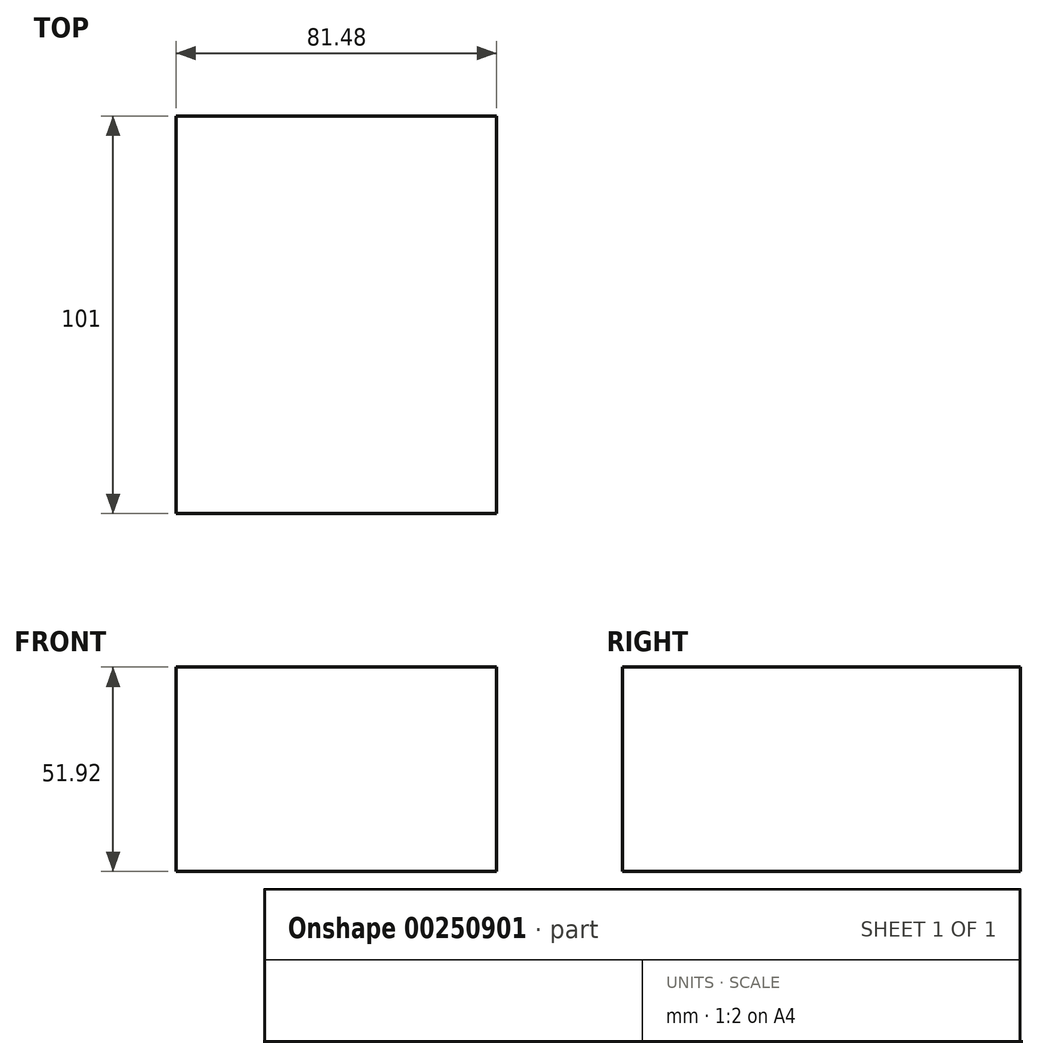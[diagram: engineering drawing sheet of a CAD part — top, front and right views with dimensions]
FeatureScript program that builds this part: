
annotation { "Feature Type Name" : "Feature", "Feature Type Description" : "" }
export const myFeature = defineFeature(function(context is Context, id is Id, definition is map)
    precondition{}
    {
        {
            var Q0;
            Q0=qCreatedBy(makeId("Front.planeOp"),FACE);
            var sketch = newSketch(context, id + "F0", { "sketchPlane" : qUnion([Q0])});
            skLineSegment(sketch, "E0.bottom", {"start": v(40.74, -25.96) * mm, "end": v(-40.74, -25.96) * mm});
            skLineSegment(sketch, "E0.top", {"start": v(40.74, 25.96) * mm, "end": v(-40.74, 25.96) * mm});
            skLineSegment(sketch, "E0.left", {"start": v(40.74, -25.96) * mm, "end": v(40.74, 25.96) * mm});
            skLineSegment(sketch, "E0.right", {"start": v(-40.74, -25.96) * mm, "end": v(-40.74, 25.96) * mm});
            skPoint(sketch, "E0.middle", {"position": v(0, 0) * mm});
            skSolve(sketch);
        }
        {
            var Q0;
            Q0=makeQuery(id+"F0.imprint","IMPRINT",FACE,{"disambiguationData":[TD([[makeQuery(id+"F0.imprint","IMPRINT",EDGE,{"derivedFrom":sQuery(id+"F0.wireOp",EDGE,"E0.bottom")}),-1.0]])]});
            extrude(context, id + "F1", {"entities" : qUnion([Q0]), "endBound" : BoundingType.SYMMETRIC, "depth" : 101 * mm});
        }
    });
